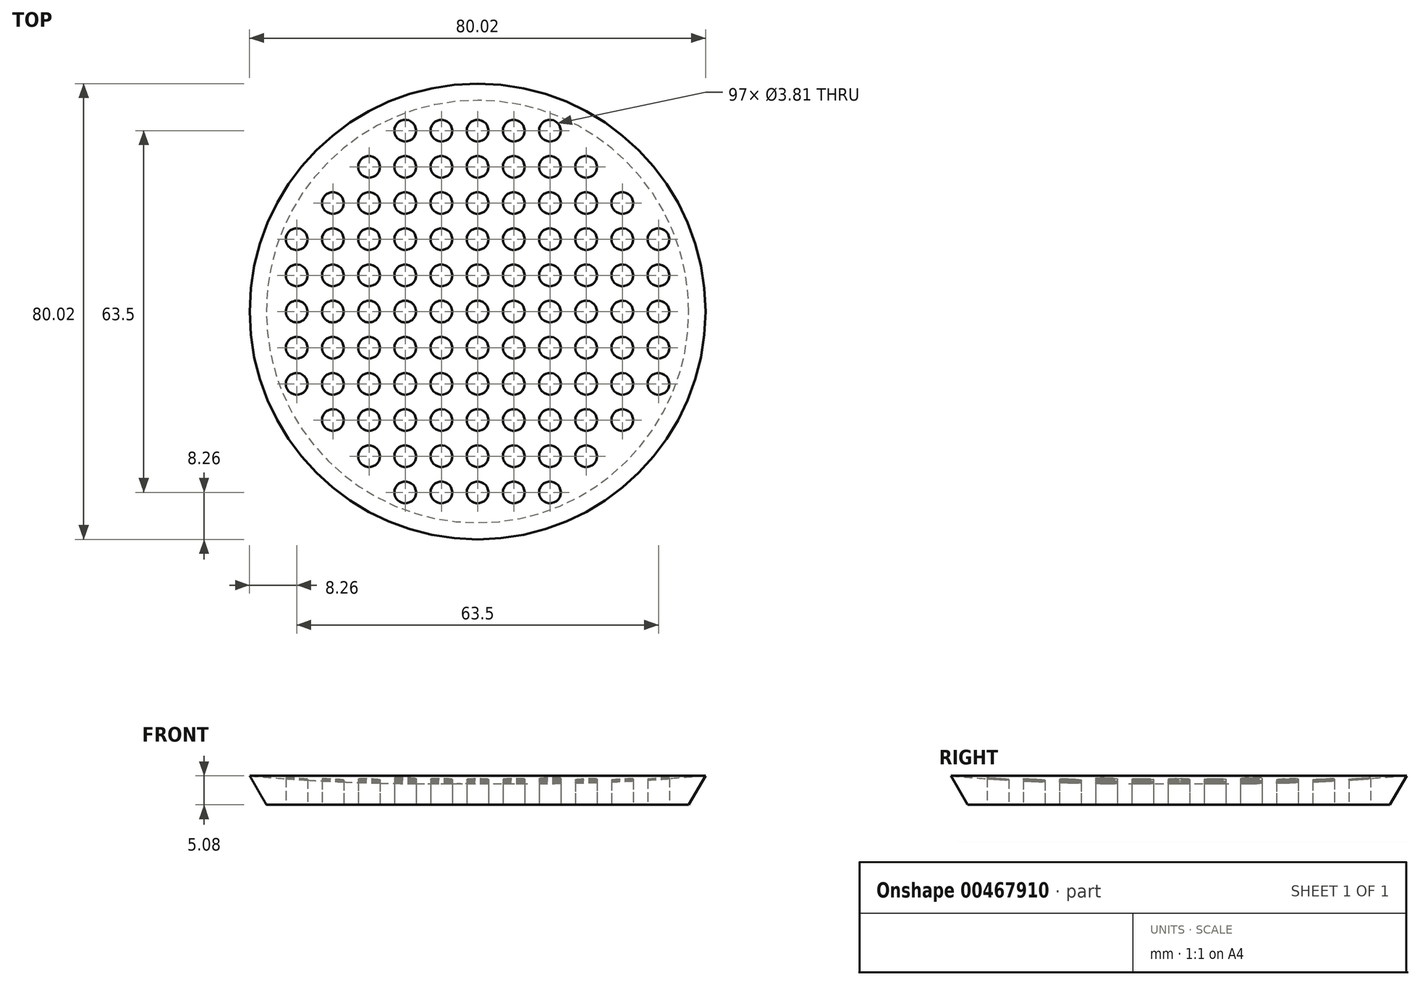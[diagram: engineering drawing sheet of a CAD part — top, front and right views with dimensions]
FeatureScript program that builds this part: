
annotation { "Feature Type Name" : "Feature", "Feature Type Description" : "" }
export const myFeature = defineFeature(function(context is Context, id is Id, definition is map)
    precondition{}
    {
        {
            var Q0;
            Q0=qCreatedBy(makeId("Front.planeOp"),FACE);
            var sketch = newSketch(context, id + "F0", { "sketchPlane" : qUnion([Q0])});
            skLineSegment(sketch, "E0", {"start": v(0, 0) * mm, "end": v(0, 3.81) * mm});
            skLineSegment(sketch, "E1", {"start": v(40, 5.08) * mm, "end": v(37.07, 0) * mm});
            skLineSegment(sketch, "E2", {"start": v(37.07, 0) * mm, "end": v(0, 0) * mm});
            skArc(sketch, "E3", {"start": v(0, 3.81) * mm, "mid": v(20.02, 3.88) * mm, "end": v(40, 5.08) * mm});
            skSolve(sketch);
        }
        {
            var Q0;
            Q0 = qSketchRegion(id + "F0", true);
            var Q1;
            Q1=sQuery(id+"F0.wireOp",EDGE,"E0");
            revolve(context, id + "F1", {"entities" : qUnion([Q0]), "axis" : qUnion([Q1]), "revolveType" : RevolveType.FULL});
        }
        {
            var Q0;
            Q0=makeQuery(id+"F1.opRevolve","SWEPT_FACE",FACE,{"disambiguationData":[OSD([sQuery(id+"F0.wireOp",EDGE,"E2")])]});
            var sketch = newSketch(context, id + "F2", { "sketchPlane" : qUnion([Q0])});
            skCircle(sketch, "E4", {"center": v(0, 0) * mm, "radius": 1.9 * mm});
            skCircle(sketch, "E5.0.1.0", {"center": v(0, 6.35) * mm, "radius": 1.9 * mm});
            skCircle(sketch, "E5.0.2.0", {"center": v(0, 12.7) * mm, "radius": 1.9 * mm});
            skCircle(sketch, "E5.0.3.0", {"center": v(0, 19.05) * mm, "radius": 1.9 * mm});
            skCircle(sketch, "E5.0.4.0", {"center": v(0, 25.4) * mm, "radius": 1.9 * mm});
            skCircle(sketch, "E5.0.5.0", {"center": v(0, 31.75) * mm, "radius": 1.9 * mm});
            skCircle(sketch, "E5.1.0.0", {"center": v(6.35, 0) * mm, "radius": 1.9 * mm});
            skCircle(sketch, "E5.1.1.0", {"center": v(6.35, 6.35) * mm, "radius": 1.9 * mm});
            skCircle(sketch, "E5.1.2.0", {"center": v(6.35, 12.7) * mm, "radius": 1.9 * mm});
            skCircle(sketch, "E5.1.3.0", {"center": v(6.35, 19.05) * mm, "radius": 1.9 * mm});
            skCircle(sketch, "E5.1.4.0", {"center": v(6.35, 25.4) * mm, "radius": 1.9 * mm});
            skCircle(sketch, "E5.1.5.0", {"center": v(6.35, 31.75) * mm, "radius": 1.9 * mm});
            skCircle(sketch, "E5.2.0.0", {"center": v(12.7, 0) * mm, "radius": 1.9 * mm});
            skCircle(sketch, "E5.2.1.0", {"center": v(12.7, 6.35) * mm, "radius": 1.9 * mm});
            skCircle(sketch, "E5.2.2.0", {"center": v(12.7, 12.7) * mm, "radius": 1.9 * mm});
            skCircle(sketch, "E5.2.3.0", {"center": v(12.7, 19.05) * mm, "radius": 1.9 * mm});
            skCircle(sketch, "E5.2.4.0", {"center": v(12.7, 25.4) * mm, "radius": 1.9 * mm});
            skCircle(sketch, "E5.2.5.0", {"center": v(12.7, 31.75) * mm, "radius": 1.9 * mm});
            skCircle(sketch, "E5.3.0.0", {"center": v(19.05, 0) * mm, "radius": 1.9 * mm});
            skCircle(sketch, "E5.3.1.0", {"center": v(19.05, 6.35) * mm, "radius": 1.9 * mm});
            skCircle(sketch, "E5.3.2.0", {"center": v(19.05, 12.7) * mm, "radius": 1.9 * mm});
            skCircle(sketch, "E5.3.3.0", {"center": v(19.05, 19.05) * mm, "radius": 1.9 * mm});
            skCircle(sketch, "E5.3.4.0", {"center": v(19.05, 25.4) * mm, "radius": 1.9 * mm});
            skCircle(sketch, "E5.4.0.0", {"center": v(25.4, 0) * mm, "radius": 1.9 * mm});
            skCircle(sketch, "E5.4.1.0", {"center": v(25.4, 6.35) * mm, "radius": 1.9 * mm});
            skCircle(sketch, "E5.4.2.0", {"center": v(25.4, 12.7) * mm, "radius": 1.9 * mm});
            skCircle(sketch, "E5.4.3.0", {"center": v(25.4, 19.05) * mm, "radius": 1.9 * mm});
            skCircle(sketch, "E5.5.0.0", {"center": v(31.75, 0) * mm, "radius": 1.9 * mm});
            skCircle(sketch, "E5.5.1.0", {"center": v(31.75, 6.35) * mm, "radius": 1.9 * mm});
            skCircle(sketch, "E5.5.2.0", {"center": v(31.75, 12.7) * mm, "radius": 1.9 * mm});
            skLineSegment(sketch, "E5.direction1", {"start": v(0, 0) * mm, "end": v(6.35, 0) * mm, "construction": true});
            skLineSegment(sketch, "E5.direction2", {"start": v(0, 0) * mm, "end": v(0, 6.35) * mm, "construction": true});
            skLineSegment(sketch, "E6.1.0.0", {"start": v(-38.1, 0) * mm, "end": v(-31.75, 0) * mm, "construction": true});
            skCircle(sketch, "E6.1.0.2", {"center": v(-12.7, 19.05) * mm, "radius": 1.9 * mm});
            skCircle(sketch, "E6.1.0.3", {"center": v(-12.7, 31.75) * mm, "radius": 1.9 * mm});
            skCircle(sketch, "E6.1.0.4", {"center": v(-19.05, 12.7) * mm, "radius": 1.9 * mm});
            skCircle(sketch, "E6.1.0.5", {"center": v(-6.35, 12.7) * mm, "radius": 1.9 * mm});
            skCircle(sketch, "E6.1.0.7", {"center": v(-12.7, 25.4) * mm, "radius": 1.9 * mm});
            skCircle(sketch, "E6.1.0.8", {"center": v(-12.7, 0) * mm, "radius": 1.9 * mm});
            skCircle(sketch, "E6.1.0.9", {"center": v(-6.35, 0) * mm, "radius": 1.9 * mm});
            skLineSegment(sketch, "E6.1.0.10", {"start": v(-38.1, 0) * mm, "end": v(-38.1, 6.35) * mm, "construction": true});
            skCircle(sketch, "E6.1.0.11", {"center": v(-19.05, 19.05) * mm, "radius": 1.9 * mm});
            skCircle(sketch, "E6.1.0.12", {"center": v(-6.35, 19.05) * mm, "radius": 1.9 * mm});
            skCircle(sketch, "E6.1.0.14", {"center": v(-25.4, 6.35) * mm, "radius": 1.9 * mm});
            skCircle(sketch, "E6.1.0.15", {"center": v(-25.4, 12.7) * mm, "radius": 1.9 * mm});
            skCircle(sketch, "E6.1.0.16", {"center": v(-25.4, 19.05) * mm, "radius": 1.9 * mm});
            skCircle(sketch, "E6.1.0.23", {"center": v(-31.75, 0) * mm, "radius": 1.9 * mm});
            skCircle(sketch, "E6.1.0.24", {"center": v(-31.75, 6.35) * mm, "radius": 1.9 * mm});
            skCircle(sketch, "E6.1.0.25", {"center": v(-31.75, 12.7) * mm, "radius": 1.9 * mm});
            skCircle(sketch, "E6.1.0.29", {"center": v(-12.7, 6.35) * mm, "radius": 1.9 * mm});
            skCircle(sketch, "E6.1.0.30", {"center": v(-25.4, 0) * mm, "radius": 1.9 * mm});
            skCircle(sketch, "E6.1.0.31", {"center": v(-6.35, 6.35) * mm, "radius": 1.9 * mm});
            skCircle(sketch, "E6.1.0.32", {"center": v(-19.05, 25.4) * mm, "radius": 1.9 * mm});
            skCircle(sketch, "E6.1.0.33", {"center": v(-6.35, 25.4) * mm, "radius": 1.9 * mm});
            skCircle(sketch, "E6.1.0.34", {"center": v(-19.05, 0) * mm, "radius": 1.9 * mm});
            skCircle(sketch, "E6.1.0.35", {"center": v(-12.7, 12.7) * mm, "radius": 1.9 * mm});
            skCircle(sketch, "E6.1.0.36", {"center": v(-6.35, 31.75) * mm, "radius": 1.9 * mm});
            skCircle(sketch, "E6.1.0.37", {"center": v(-19.05, 6.35) * mm, "radius": 1.9 * mm});
            skLineSegment(sketch, "E6.direction1", {"start": v(0, 0) * mm, "end": v(-38.1, 0) * mm, "construction": true});
            skCircle(sketch, "E7.0.1.0", {"center": v(-31.75, -6.35) * mm, "radius": 1.9 * mm});
            skCircle(sketch, "E7.0.1.1", {"center": v(-19.05, -12.7) * mm, "radius": 1.9 * mm});
            skCircle(sketch, "E7.0.1.2", {"center": v(-6.35, -25.4) * mm, "radius": 1.9 * mm});
            skCircle(sketch, "E7.0.1.5", {"center": v(-25.4, -19.05) * mm, "radius": 1.9 * mm});
            skCircle(sketch, "E7.0.1.6", {"center": v(25.4, -19.05) * mm, "radius": 1.9 * mm});
            skCircle(sketch, "E7.0.1.7", {"center": v(-6.35, -19.05) * mm, "radius": 1.9 * mm});
            skCircle(sketch, "E7.0.1.10", {"center": v(19.05, -12.7) * mm, "radius": 1.9 * mm});
            skCircle(sketch, "E7.0.1.13", {"center": v(31.75, -12.7) * mm, "radius": 1.9 * mm});
            skCircle(sketch, "E7.0.1.15", {"center": v(-6.35, -12.7) * mm, "radius": 1.9 * mm});
            skCircle(sketch, "E7.0.1.17", {"center": v(-6.35, -6.35) * mm, "radius": 1.9 * mm});
            skCircle(sketch, "E7.0.1.18", {"center": v(-19.05, -6.35) * mm, "radius": 1.9 * mm});
            skCircle(sketch, "E7.0.1.21", {"center": v(-12.7, -6.35) * mm, "radius": 1.9 * mm});
            skCircle(sketch, "E7.0.1.23", {"center": v(-12.7, -25.4) * mm, "radius": 1.9 * mm});
            skCircle(sketch, "E7.0.1.25", {"center": v(6.35, -6.35) * mm, "radius": 1.9 * mm});
            skCircle(sketch, "E7.0.1.26", {"center": v(6.35, -12.7) * mm, "radius": 1.9 * mm});
            skCircle(sketch, "E7.0.1.27", {"center": v(6.35, -19.05) * mm, "radius": 1.9 * mm});
            skCircle(sketch, "E7.0.1.28", {"center": v(6.35, -25.4) * mm, "radius": 1.9 * mm});
            skCircle(sketch, "E7.0.1.29", {"center": v(6.35, -31.75) * mm, "radius": 1.9 * mm});
            skCircle(sketch, "E7.0.1.31", {"center": v(19.05, -6.35) * mm, "radius": 1.9 * mm});
            skCircle(sketch, "E7.0.1.32", {"center": v(0, -6.35) * mm, "radius": 1.9 * mm});
            skCircle(sketch, "E7.0.1.33", {"center": v(0, -12.7) * mm, "radius": 1.9 * mm});
            skCircle(sketch, "E7.0.1.34", {"center": v(0, -19.05) * mm, "radius": 1.9 * mm});
            skCircle(sketch, "E7.0.1.35", {"center": v(0, -25.4) * mm, "radius": 1.9 * mm});
            skCircle(sketch, "E7.0.1.36", {"center": v(0, -31.75) * mm, "radius": 1.9 * mm});
            skCircle(sketch, "E7.0.1.40", {"center": v(12.7, -19.05) * mm, "radius": 1.9 * mm});
            skCircle(sketch, "E7.0.1.42", {"center": v(-6.35, -31.75) * mm, "radius": 1.9 * mm});
            skCircle(sketch, "E7.0.1.43", {"center": v(-19.05, -25.4) * mm, "radius": 1.9 * mm});
            skLineSegment(sketch, "E7.0.1.45", {"start": v(0, -38.1) * mm, "end": v(0, -31.75) * mm, "construction": true});
            skCircle(sketch, "E7.0.1.46", {"center": v(31.75, -6.35) * mm, "radius": 1.9 * mm});
            skCircle(sketch, "E7.0.1.49", {"center": v(25.4, -12.7) * mm, "radius": 1.9 * mm});
            skCircle(sketch, "E7.0.1.50", {"center": v(-12.7, -31.75) * mm, "radius": 1.9 * mm});
            skCircle(sketch, "E7.0.1.51", {"center": v(-25.4, -12.7) * mm, "radius": 1.9 * mm});
            skCircle(sketch, "E7.0.1.52", {"center": v(19.05, -19.05) * mm, "radius": 1.9 * mm});
            skCircle(sketch, "E7.0.1.56", {"center": v(12.7, -12.7) * mm, "radius": 1.9 * mm});
            skCircle(sketch, "E7.0.1.57", {"center": v(12.7, -25.4) * mm, "radius": 1.9 * mm});
            skCircle(sketch, "E7.0.1.58", {"center": v(-25.4, -6.35) * mm, "radius": 1.9 * mm});
            skCircle(sketch, "E7.0.1.59", {"center": v(12.7, -31.75) * mm, "radius": 1.9 * mm});
            skCircle(sketch, "E7.0.1.62", {"center": v(-19.05, -19.05) * mm, "radius": 1.9 * mm});
            skCircle(sketch, "E7.0.1.63", {"center": v(-31.75, -12.7) * mm, "radius": 1.9 * mm});
            skCircle(sketch, "E7.0.1.65", {"center": v(-12.7, -12.7) * mm, "radius": 1.9 * mm});
            skCircle(sketch, "E7.0.1.68", {"center": v(-12.7, -19.05) * mm, "radius": 1.9 * mm});
            skCircle(sketch, "E7.0.1.71", {"center": v(19.05, -25.4) * mm, "radius": 1.9 * mm});
            skCircle(sketch, "E7.0.1.72", {"center": v(25.4, -6.35) * mm, "radius": 1.9 * mm});
            skCircle(sketch, "E7.0.1.75", {"center": v(12.7, -6.35) * mm, "radius": 1.9 * mm});
            skLineSegment(sketch, "E7.0.1.76", {"start": v(0, -38.1) * mm, "end": v(6.35, -38.1) * mm, "construction": true});
            skLineSegment(sketch, "E7.direction1", {"start": v(-38.1, 0) * mm, "end": v(-12.7, 0) * mm, "construction": true});
            skSolve(sketch);
        }
        {
            var Q0;
            Q0 = qSketchRegion(id + "F2", true);
            extrude(context, id + "F3", {"entities" : qUnion([Q0]), "operationType" : NewBodyOperationType.REMOVE, "endBound" : BoundingType.THROUGH_ALL, "oppositeDirection" : true, "depth" : 25.4 * mm});
        }
    });
